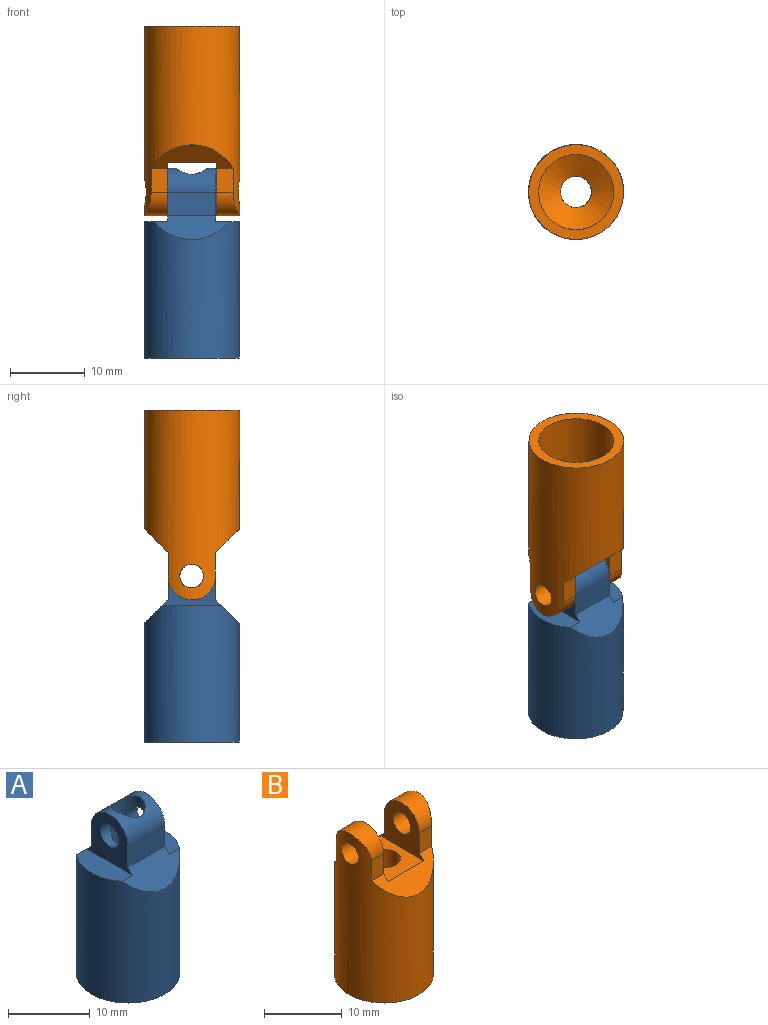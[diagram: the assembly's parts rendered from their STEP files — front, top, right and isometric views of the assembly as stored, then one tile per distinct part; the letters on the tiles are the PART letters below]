
ASSEMBLY  parts=2 mates=1
PART A: 16 faces, bbox 12.7x12.7x25.4 mm
  f0: cylinder r=2.1mm len=15mm, axis (0,0,-1), area 175.4mm2, adj f1,f2,f3,f14
  f1: cylinder r=3.17mm len=6.38mm, axis (1,0,0), area 48.8mm2, adj f0,f5,f8,f11,f13
  f2: cylinder r=1.59mm len=3.18mm, axis (1,0,0), area 14.3mm2, adj f0,f13
  f3: cylinder r=1.59mm len=3.18mm, axis (1,0,0), area 14.3mm2, adj f0,f11
  f4: cylinder r=6.35mm len=18.26mm, axis (0,0,1), area 692.8mm2, adj f6,f7,f9,f10,f12
  f5: plane 6.38x3.18mm, normal (0,1,0), area 20.2mm2, adj f1,f6,f11,f13
  f6: plane 9.91x3.18mm, normal (0,0.71,0.71), area 30.4mm2, adj f4,f5,f10,f11,f12,f13
  f7: plane 9.91x3.18mm, normal (0,-0.71,0.71), area 30.4mm2, adj f4,f8,f10,f11,f12,f13
  f8: plane 6.38x3.18mm, normal (0,-1,0), area 20.2mm2, adj f1,f7,f11,f13
  f9: plane 12.7x12.7mm, normal (0,0,-1), area 46.8mm2, adj f4,f15
  f10: plane 7.94x3.16mm, normal (0,0,1), area 21.6mm2, adj f4,f6,f7,f11
  f11: plane 7.94x7.14mm, normal (1,0,0), area 33.7mm2, adj f1,f3,f5,f6,f7,f8,f10
  f12: plane 7.94x3.16mm, normal (0,0,1), area 21.6mm2, adj f4,f6,f7,f13
  f13: plane 7.94x7.14mm, normal (-1,0,0), area 33.7mm2, adj f1,f2,f5,f6,f7,f8,f12
  f14: cone r=0mm half-angle=59deg, axis (0,0,-1), area 77mm2, adj f0,f15
  f15: cylinder r=5.04mm len=10.08mm, axis (0,0,-1), area 273.6mm2, adj f9,f14
PART B: 18 faces, bbox 12.7x12.7x25.4 mm
  f0: cylinder r=2.1mm len=7.85mm, axis (0,0,-1), area 103.6mm2, adj f13,f16
  f1: cylinder r=3.17mm len=6.35mm, axis (1,0,0), area 26.9mm2, adj f2,f5,f7,f14
  f2: plane 3.18x2.26mm, normal (0,1,0), area 7.2mm2, adj f1,f3,f7,f14
  f3: plane 11x3.18mm, normal (0,0.71,0.71), area 27.8mm2, adj f2,f7,f10,f13,f14,f15
  f4: plane 11x3.18mm, normal (0,-0.71,0.71), area 27.8mm2, adj f5,f7,f11,f13,f14,f15
  f5: plane 3.18x2.26mm, normal (0,-1,0), area 7.2mm2, adj f1,f4,f7,f14
  f6: cylinder r=1.59mm len=3.18mm, axis (1,0,0), area 30.1mm2, adj f7,f14
  f7: cylinder r=6.35mm len=25.4mm, axis (0,0,1), area 763.8mm2, adj f1,f2,f3,f4,f5,f6,f8,f9
  f8: plane 12.7x12.7mm, normal (0,0,-1), area 46.8mm2, adj f7,f17
  f9: cylinder r=3.17mm len=6.35mm, axis (1,0,0), area 26.9mm2, adj f7,f10,f11,f15
  f10: plane 3.18x2.26mm, normal (0,1,0), area 7.2mm2, adj f3,f7,f9,f15
  f11: plane 3.18x2.26mm, normal (0,-1,0), area 7.2mm2, adj f4,f7,f9,f15
  f12: cylinder r=1.59mm len=3.18mm, axis (1,0,0), area 30.1mm2, adj f7,f15
  f13: plane 7.94x6.48mm, normal (0,0,1), area 37.6mm2, adj f0,f3,f4,f14,f15
  f14: plane 7.94x7.14mm, normal (1,0,0), area 33.7mm2, adj f1,f2,f3,f4,f5,f6,f13
  f15: plane 7.94x7.14mm, normal (-1,0,0), area 33.7mm2, adj f3,f4,f9,f10,f11,f12,f13
  f16: cone r=0mm half-angle=59deg, axis (0,0,-1), area 77mm2, adj f0,f17
  f17: cylinder r=5.04mm len=10.08mm, axis (0,0,-1), area 273.6mm2, adj f8,f16
PLACE A t=(3.01,37.35,47.69)mm fixed
PLACE B rot(axis=(0,-1,0),180deg) t=(3.06,37.35,47.69)mm
MATE revolute B.f6 <-> A.f1  axis (-1,0,0) through (-0.18,37.35,47.69)mm
